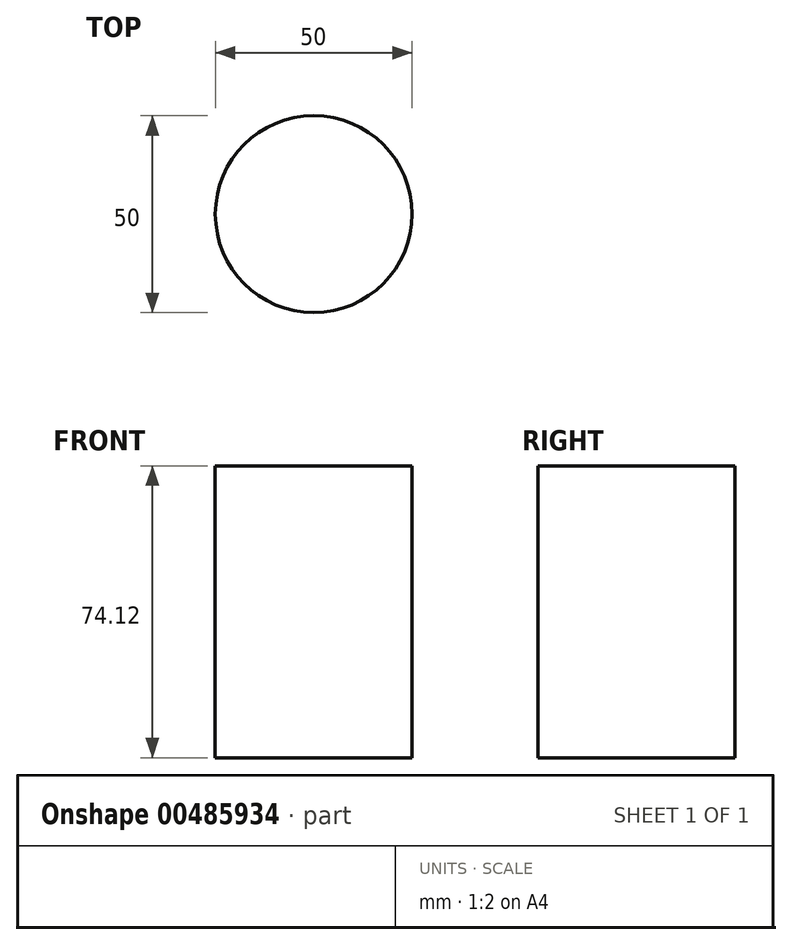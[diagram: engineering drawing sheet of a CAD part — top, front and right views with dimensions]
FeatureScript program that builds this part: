
annotation { "Feature Type Name" : "Feature", "Feature Type Description" : "" }
export const myFeature = defineFeature(function(context is Context, id is Id, definition is map)
    precondition{}
    {
        {
            var Q0;
            Q0=qCreatedBy(makeId("Top.planeOp"),FACE);
            var sketch = newSketch(context, id + "F0", { "sketchPlane" : qUnion([Q0])});
            skCircle(sketch, "E0", {"center": v(20.86, 0) * mm, "radius": 25 * mm});
            skSolve(sketch);
        }
        {
            var Q0;
            Q0 = qSketchRegion(id + "F0", true);
            extrude(context, id + "F1", {"entities" : qUnion([Q0]), "depth" : 74.12 * mm});
        }
    });
